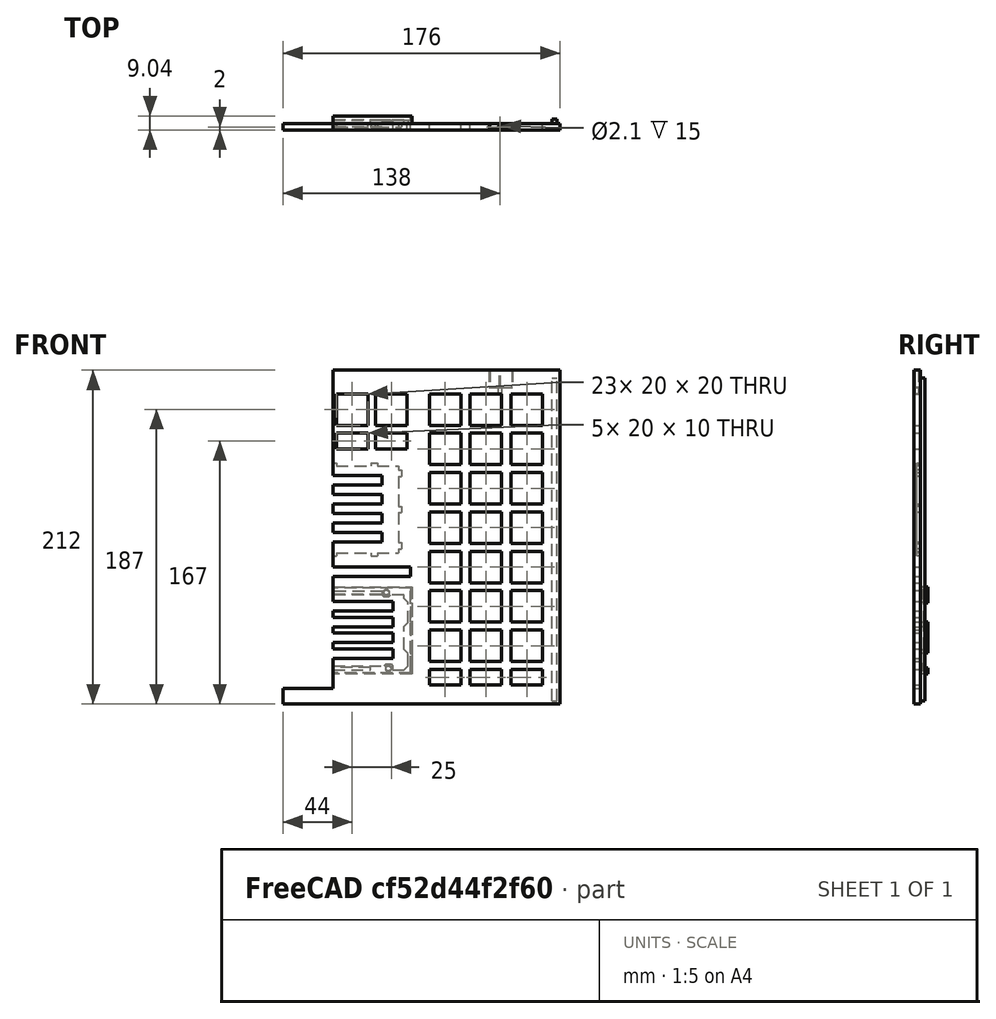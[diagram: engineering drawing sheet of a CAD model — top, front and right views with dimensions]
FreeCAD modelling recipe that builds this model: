
FCSTD DOCUMENT  (FreeCAD 0.17R13522 (Git))
Label: base_para_arduino_y_matrizia_derecha
License: CreativeCommons Attribution-ShareAlike
LicenseURL: http://creativecommons.org/licenses/by-sa/4.0/
objects: Part::Feature×3, Part::Cut×2, Part::Fuse×1, Part::Box×1
note: 7 computed .brp shape members not serialized (recipe doc carries the construction recipe); baked Part::Feature solids carry a one-line shape summary decoded from their .brp

FEATURE [Part::Feature] Cut001001001002003001008002002034017001  label="Cut001001001002003001008002002034018"
  shape: bbox 92 x 7 x 212 mm, 109 faces (baked)
FEATURE [Part::Feature] Cut001001001002003001008002002034017002  label="Cut001001001002003001008002002034019"
  shape: bbox 85 x 9.04 x 212 mm, 370 faces (baked)
FEATURE [Part::Fuse] Fusion
  Base = -> Cut001001001002003001008002002034017001
  Refine = true
  Tool = -> Cut001001001002003001008002002034017002
FEATURE [Part::Feature] Body001  label="cortador_parea_encastres"
  Placement = pos=(682,-52,-462) rot=(0,0,1;0rad)
  shape: bbox 15 x 2 x 20 mm, 6 faces (baked)
FEATURE [Part::Cut] Cut
  Base = -> Fusion
  Tool = -> Body001
FEATURE [Part::Box] Box  label="Cube"
  AttacherType = Attacher::AttachEngine3D
  Height = 20
  Length = 14
  Placement = pos=(681.5,-52,-462) rot=(0,0,1;0rad)
  Width = 10
FEATURE [Part::Cut] Cut001001001002003001008002002034017003  label="base derecha"
  Base = -> Cut
  Tool = -> Box
